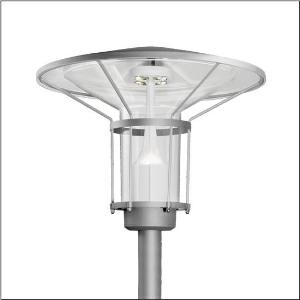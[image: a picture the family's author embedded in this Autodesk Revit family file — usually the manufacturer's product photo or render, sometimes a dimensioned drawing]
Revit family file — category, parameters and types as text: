
# Revit family: laterne_classic_iq___st1_2a_5xa5245af14h_9f1a
name_source: partatom
category: Lighting Fixtures
units: mm (PartAtom-declared; Revit-internal decimal feet)

## family parameters
Cut with Voids When Loaded = No
Host = Face
Light Source = No
Part Type = Normal
Room Calculation Point = No
Round Connector Dimension = Use Diameter
Shared = No

## types (1)
- --- (1 x LED, 1380 lm, 12.9 W, 2200K)
    Apparent Load = 13 VA
    CIE Flux Codes = 21 60 93 97 100
    Color Rendering = 70
    Color Temperature = 2200K
    Default Elevation = 1800 mm
    Description = Lantern Classic iQ, mast luminaire, Module 540 iQ-SR, primary light control with 3 zone facetted reflector, of plastic, silver coated, highly specular, structured, primary optical cover: cover, of PMMA, transparent, light distribution: ST1.2a, light emission: direct distribution, primary light characteristic: asymmetric, installation type: post-top, LED, High Power LED, rated luminous flux: 1.380lm, luminous efficacy: 107lm/W, light colour: 722, colour temperature: 2200K, control gear: ECG iQ, control: pre-setting: logarithmic dimming characteristic, Street-Remote, Auto-Match, Temp-Guard, Lumen-Switch, Night-Set, Smart-Wire, Light-Fading, Desk-Remote (wireless, voltage-free reading and setting of iQ features in the workshop via application-optimized NFC function/RFID function), optimised constant luminous flux control (CLO 2.0), with terminal, 6-pole, max. 2.5mm², mains connection: 230..240V, AC, 50/60Hz, start of lifetime: 13W, end of service life: 13W, reduction: 6W, luminaire housing, upper part, of glass-fibre reinforced polyester, coated, Siteco® metallic grey (DB 702S), diameter: 750mm, height: 596mm, spigot size: d x l = 76 x 70mm (post-top) | with reducer (optional accessory) 60 x 70mm, post-top mast mounting element, of diecast aluminium, coated, Siteco® metallic grey (DB 702S), Module 540 iQ-SR, traffic white (RAL 9016), equipment: standard, protection rating (complete): IP65, insulation class (complete): insulation class II (safety insulation), certification: CE, ENEC, VDE, packaging unit: 1 piece

Light Distribution: ST1.2a
    Height = 596 mm
    Lamp = 1 x LED
    Lamp Light Flux = 1380 lm
    Lamp Power = 12.9 W
    Lamp count = 1
    Length = 750 mm
    Luminous efficacy = 107 lm/W
    Manufacturer = Siteco
    ModVariant = No
    Model = 5XA5245AF14H
    Number of Poles = 1
    OnlyDefault = Yes
    Power Factor = 1
    Product Name = Laterne Classic iQ | ST1.2a
    Product group = mast luminaire | pylon top
    ProductGroupID = 6100
    Protection Class = Protection class II
    Protection Degree = IP 65
    RLX_Detail_Level = 1
    RLX_Emergency_Light_Flux = 0 lm
    RLX_Emergency_Type = 0
    RLX_Emergency_Type_DB = No
    RlxData = <blob elided: 92073 chars, md5=4563de2a>
    Socket = socket
    Standby Power = 0 W
    System Light Flux = 1380 lm
    System Power = 13 W
    Type Comments = factory setting: luminous flux: 100 % | dim-lin: 254 | 516 mA
    Type Image = l_1006052.jpg
    URL = http://relux.com
    VarID = @adj_130765
    Voltage = 0 V
    Weight = 0.00 kg
    Width = 0 mm  [stored 0 ft]

note: [stored X ft] marks values corroborated as IEEE doubles in the binary element streams (Revit-internal decimal feet)

## geometry (parser evidence)
native form markers: Blend x4, Sweep x13
no freeform markers — native parametric forms only
